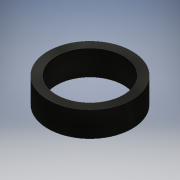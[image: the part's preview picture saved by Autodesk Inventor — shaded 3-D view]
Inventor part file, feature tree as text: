
AUTODESK INVENTOR PART (.ipt)
format: ipt  version: 2016 (Build 200138000, 138)  size: 98,304 bytes
history: native  units: mm
features: other x1, extrude x1, sketch x1
ambient origin geometry x8: Origin, YZ Plane, XZ Plane, XY Plane, X Axis, Y Axis, Z Axis, Center Point
bodies: Body1 (feature_tree)
feature tree (3):
  other  "ソリッド1"
  extrude  "押し出し1"  Depth=8.0mm
  sketch  "スケッチ1"
